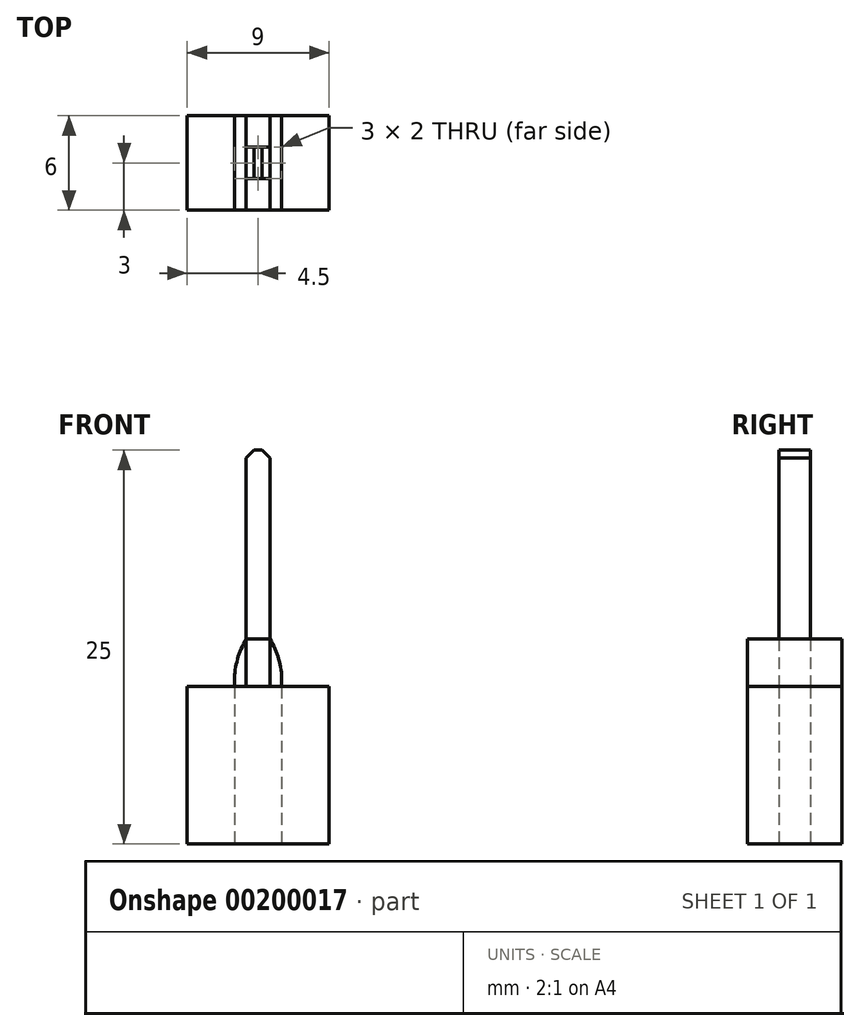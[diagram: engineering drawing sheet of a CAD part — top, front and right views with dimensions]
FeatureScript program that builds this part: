
annotation { "Feature Type Name" : "Feature", "Feature Type Description" : "" }
export const myFeature = defineFeature(function(context is Context, id is Id, definition is map)
    precondition{}
    {
        {
            var Q0;
            Q0=qCreatedBy(makeId("Top.planeOp"),FACE);
            var sketch = newSketch(context, id + "F0", { "sketchPlane" : qUnion([Q0])});
            skLineSegment(sketch, "E0.bottom", {"start": v(0, 0) * mm, "end": v(9, 0) * mm});
            skLineSegment(sketch, "E0.top", {"start": v(0, 6) * mm, "end": v(9, 6) * mm});
            skLineSegment(sketch, "E0.left", {"start": v(0, 0) * mm, "end": v(0, 6) * mm});
            skLineSegment(sketch, "E0.right", {"start": v(9, 0) * mm, "end": v(9, 6) * mm});
            skLineSegment(sketch, "E1.bottom", {"start": v(3, 2) * mm, "end": v(6, 2) * mm});
            skLineSegment(sketch, "E1.top", {"start": v(3, 4) * mm, "end": v(6, 4) * mm});
            skLineSegment(sketch, "E1.left", {"start": v(3, 2) * mm, "end": v(3, 4) * mm});
            skLineSegment(sketch, "E1.right", {"start": v(6, 2) * mm, "end": v(6, 4) * mm});
            skSolve(sketch);
        }
        {
            var Q0;
            Q0=makeQuery(id+"F0.imprint","IMPRINT",FACE,{"disambiguationData":[TD([[makeQuery(id+"F0.imprint","IMPRINT",EDGE,{"derivedFrom":sQuery(id+"F0.wireOp",EDGE,"E0.bottom")}),1.0]])]});
            extrude(context, id + "F1", {"entities" : qUnion([Q0]), "depth" : 10 * mm});
        }
        {
            var Q0;
            Q0=makeQuery(id+"F1.opExtrude","CAP_FACE",FACE,{"disambiguationData":[OSD([sQuery(id+"F0.wireOp",EDGE,"E0.bottom"),sQuery(id+"F0.wireOp",EDGE,"E0.top"),sQuery(id+"F0.wireOp",EDGE,"E0.left"),sQuery(id+"F0.wireOp",EDGE,"E0.right"),sQuery(id+"F0.wireOp",EDGE,"E1.bottom"),sQuery(id+"F0.wireOp",EDGE,"E1.top"),sQuery(id+"F0.wireOp",EDGE,"E1.left"),sQuery(id+"F0.wireOp",EDGE,"E1.right")])],"isStart":false});
            var sketch = newSketch(context, id + "F2", { "sketchPlane" : qUnion([Q0])});
            skLineSegment(sketch, "E2.bottom", {"start": v(3, 6) * mm, "end": v(6, 6) * mm});
            skLineSegment(sketch, "E2.top", {"start": v(3, 0) * mm, "end": v(6, 0) * mm});
            skLineSegment(sketch, "E2.left", {"start": v(3, 6) * mm, "end": v(3, 0) * mm});
            skLineSegment(sketch, "E2.right", {"start": v(6, 6) * mm, "end": v(6, 0) * mm});
            skLineSegment(sketch, "E3.bottom", {"start": v(3.75, 6) * mm, "end": v(5.25, 6) * mm});
            skLineSegment(sketch, "E3.top", {"start": v(3.75, 0) * mm, "end": v(5.25, 0) * mm});
            skLineSegment(sketch, "E3.left", {"start": v(3.75, 6) * mm, "end": v(3.75, 0) * mm});
            skLineSegment(sketch, "E3.right", {"start": v(5.25, 6) * mm, "end": v(5.25, 0) * mm});
            skSolve(sketch);
        }
        {
            var Q0;
            {var subQ0=sQuery(id+"F2.wireOp",EDGE,"E3.bottom");Q0=makeQuery(id+"F2.imprint","IMPRINT",FACE,{"disambiguationData":[TD([[makeQuery(id+"F2.imprint","IMPRINT",EDGE,{"derivedFrom":subQ0}),-1.0]])]});}
            var Q1;
            {var subQ0=sQuery(id+"F2.wireOp",EDGE,"E3.top");Q1=makeQuery(id+"F2.imprint","IMPRINT",FACE,{"disambiguationData":[TD([[makeQuery(id+"F2.imprint","IMPRINT",EDGE,{"derivedFrom":subQ0}),1.0]])]});}
            var Q2;
            {var subQ0=sQuery(id+"F2.wireOp",EDGE,"E3.left");var subQ1=makeQuery(id+"F1.opExtrude","CAP_EDGE",EDGE,{"disambiguationData":[OSD([sQuery(id+"F0.wireOp",EDGE,"E1.top")])],"isStart":false});var subQ2=makeQuery(id+"F2.imprint","INTERSECT",VERTEX,{"derivedFrom":[subQ1,subQ0]});Q2=makeQuery(id+"F2.imprint","IMPRINT",FACE,{"disambiguationData":[TD([[makeQuery(id+"F2.imprint","IMPRINT",EDGE,{"disambiguationData":[TD([[subQ2,-1.0]])],"derivedFrom":subQ0}),1.0]])]});}
            extrude(context, id + "F3", {"entities" : qUnion([Q0, Q1, Q2]), "operationType" : NewBodyOperationType.ADD, "depth" : 15 * mm});
        }
        {
            var Q0;
            {var subQ0=sQuery(id+"F2.wireOp",EDGE,"E2.left");var subQ5=makeQuery(id+"F1.opExtrude","CAP_EDGE",EDGE,{"disambiguationData":[OSD([sQuery(id+"F0.wireOp",EDGE,"E1.bottom")])],"isStart":false});var subQ6=makeQuery(id+"F2.imprint","INTERSECT",VERTEX,{"derivedFrom":[subQ5,subQ0]});Q0=makeQuery(id+"F2.imprint","IMPRINT",FACE,{"disambiguationData":[TD([[makeQuery(id+"F2.imprint","IMPRINT",EDGE,{"disambiguationData":[TD([[subQ6,-1.0]])],"derivedFrom":subQ5}),-1.0]])]});}
            var Q1;
            {var subQ0=sQuery(id+"F2.wireOp",EDGE,"E2.left");var subQ1=makeQuery(id+"F1.opExtrude","CAP_EDGE",EDGE,{"disambiguationData":[OSD([sQuery(id+"F0.wireOp",EDGE,"E1.bottom")])],"isStart":false});var subQ2=makeQuery(id+"F2.imprint","INTERSECT",VERTEX,{"derivedFrom":[subQ1,subQ0]});var subQ3=makeQuery(id+"F1.opExtrude","CAP_EDGE",EDGE,{"disambiguationData":[OSD([sQuery(id+"F0.wireOp",EDGE,"E1.top")])],"isStart":false});var subQ4=makeQuery(id+"F2.imprint","INTERSECT",VERTEX,{"derivedFrom":[subQ3,subQ0]});Q1=makeQuery(id+"F2.imprint","IMPRINT",FACE,{"disambiguationData":[TD([[makeQuery(id+"F2.imprint","IMPRINT",EDGE,{"disambiguationData":[TD([[subQ2,-1.0],[subQ4,1.0]])],"derivedFrom":subQ0}),-1.0]])]});}
            var Q2;
            {var subQ0=sQuery(id+"F2.wireOp",EDGE,"E2.left");var subQ5=makeQuery(id+"F1.opExtrude","CAP_EDGE",EDGE,{"disambiguationData":[OSD([sQuery(id+"F0.wireOp",EDGE,"E1.top")])],"isStart":false});var subQ6=makeQuery(id+"F2.imprint","INTERSECT",VERTEX,{"derivedFrom":[subQ5,subQ0]});Q2=makeQuery(id+"F2.imprint","IMPRINT",FACE,{"disambiguationData":[TD([[makeQuery(id+"F2.imprint","IMPRINT",EDGE,{"disambiguationData":[TD([[subQ6,-1.0]])],"derivedFrom":subQ5}),1.0]])]});}
            var Q3;
            {var subQ0=sQuery(id+"F2.wireOp",EDGE,"E2.right");var subQ5=makeQuery(id+"F1.opExtrude","CAP_EDGE",EDGE,{"disambiguationData":[OSD([sQuery(id+"F0.wireOp",EDGE,"E1.top")])],"isStart":false});var subQ6=makeQuery(id+"F2.imprint","INTERSECT",VERTEX,{"derivedFrom":[subQ5,subQ0]});Q3=makeQuery(id+"F2.imprint","IMPRINT",FACE,{"disambiguationData":[TD([[makeQuery(id+"F2.imprint","IMPRINT",EDGE,{"disambiguationData":[TD([[subQ6,1.0]])],"derivedFrom":subQ5}),1.0]])]});}
            var Q4;
            {var subQ0=sQuery(id+"F2.wireOp",EDGE,"E2.right");var subQ1=makeQuery(id+"F1.opExtrude","CAP_EDGE",EDGE,{"disambiguationData":[OSD([sQuery(id+"F0.wireOp",EDGE,"E1.bottom")])],"isStart":false});var subQ2=makeQuery(id+"F2.imprint","INTERSECT",VERTEX,{"derivedFrom":[subQ1,subQ0]});var subQ3=makeQuery(id+"F1.opExtrude","CAP_EDGE",EDGE,{"disambiguationData":[OSD([sQuery(id+"F0.wireOp",EDGE,"E1.top")])],"isStart":false});var subQ4=makeQuery(id+"F2.imprint","INTERSECT",VERTEX,{"derivedFrom":[subQ3,subQ0]});Q4=makeQuery(id+"F2.imprint","IMPRINT",FACE,{"disambiguationData":[TD([[makeQuery(id+"F2.imprint","IMPRINT",EDGE,{"disambiguationData":[TD([[subQ2,-1.0],[subQ4,1.0]])],"derivedFrom":subQ0}),1.0]])]});}
            var Q5;
            {var subQ0=sQuery(id+"F2.wireOp",EDGE,"E2.right");var subQ5=makeQuery(id+"F1.opExtrude","CAP_EDGE",EDGE,{"disambiguationData":[OSD([sQuery(id+"F0.wireOp",EDGE,"E1.bottom")])],"isStart":false});var subQ6=makeQuery(id+"F2.imprint","INTERSECT",VERTEX,{"derivedFrom":[subQ5,subQ0]});Q5=makeQuery(id+"F2.imprint","IMPRINT",FACE,{"disambiguationData":[TD([[makeQuery(id+"F2.imprint","IMPRINT",EDGE,{"disambiguationData":[TD([[subQ6,1.0]])],"derivedFrom":subQ5}),-1.0]])]});}
            extrude(context, id + "F4", {"entities" : qUnion([Q0, Q1, Q2, Q3, Q4, Q5]), "depth" : 3 * mm});
        }
        {
            var Q0;
            Q0=makeQuery(id+"F4.opExtrude","CAP_EDGE",EDGE,{"disambiguationData":[OSD([sQuery(id+"F2.wireOp",EDGE,"E2.left")])],"isStart":false});
            var Q1;
            Q1=makeQuery(id+"F4.opExtrude","CAP_EDGE",EDGE,{"disambiguationData":[OSD([sQuery(id+"F2.wireOp",EDGE,"E2.right")])],"isStart":false});
            var Q2;
            Q2=makeQuery(id+"F3.opExtrude","CAP_EDGE",EDGE,{"disambiguationData":[OSD([sQuery(id+"F2.wireOp",EDGE,"E3.top")])],"isStart":false});
            fillet(context, id + "F5", {"entities" : qUnion([Q0, Q1, Q2]), "radius" : 5 * mm, "tangentPropagation" : true, "allowEdgeOverflow" : false});
        }
        {
            var Q0;
            Q0=makeQuery(id+"F3.opExtrude","CAP_EDGE",EDGE,{"disambiguationData":[OSD([sQuery(id+"F2.wireOp",EDGE,"E3.left")])],"isStart":false});
            var Q1;
            Q1=makeQuery(id+"F3.opExtrude","CAP_EDGE",EDGE,{"disambiguationData":[OSD([sQuery(id+"F2.wireOp",EDGE,"E3.right")])],"isStart":false});
            chamfer(context, id + "F6", {"entities" : qUnion([Q0, Q1]), "chamferType" : ChamferType.OFFSET_ANGLE, "width" : 0.5 * mm, "oppositeDirection" : true, "angle" : 45 * degree, "tangentPropagation" : true});
        }
        {
            var Q0;
            Q0=makeQuery(id+"F4.opExtrude","SWEPT_FACE",FACE,{"disambiguationData":[OSD([sQuery(id+"F2.wireOp",EDGE,"E3.right")])]});
            var Q1;
            Q1=makeQuery(id+"F4.opExtrude","SWEPT_FACE",FACE,{"disambiguationData":[OSD([sQuery(id+"F2.wireOp",EDGE,"E3.left")])]});
            loft(context, id + "F7", {"sheetProfilesArray" : [{ "sheetProfileEntities" : qUnion([Q0]) }, { "sheetProfileEntities" : qUnion([Q1]) }]});
        }
    });
